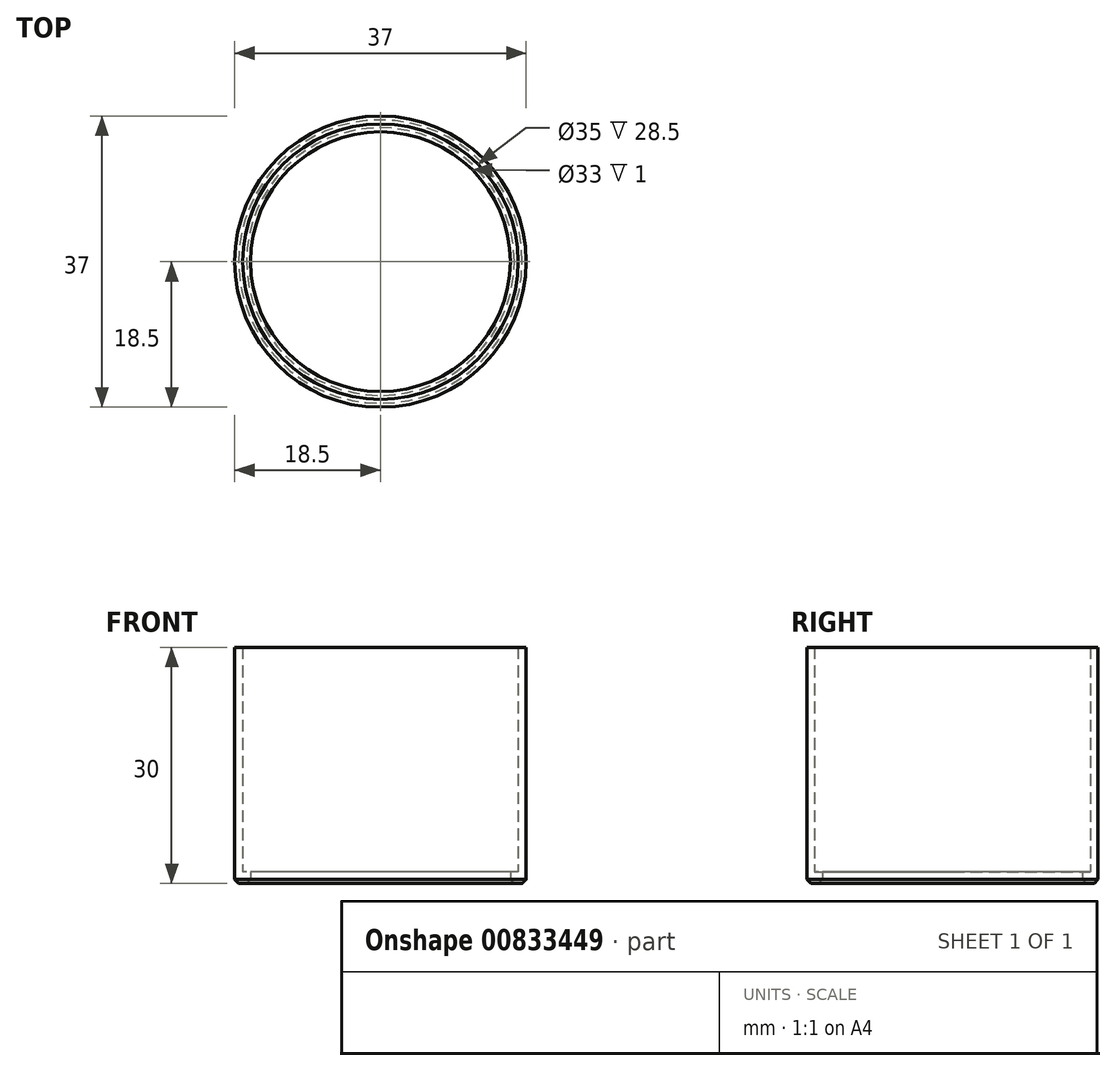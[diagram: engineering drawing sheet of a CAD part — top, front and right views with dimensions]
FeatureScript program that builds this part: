
annotation { "Feature Type Name" : "Feature", "Feature Type Description" : "" }
export const myFeature = defineFeature(function(context is Context, id is Id, definition is map)
    precondition{}
    {
        {
            var Q0;
            Q0=qCreatedBy(makeId("Top.planeOp"),FACE);
            var sketch = newSketch(context, id + "F0", { "sketchPlane" : qUnion([Q0])});
            skCircle(sketch, "E0", {"center": v(0, 0) * mm, "radius": 16.5 * mm});
            skCircle(sketch, "E1", {"center": v(0, 0) * mm, "radius": 17.5 * mm});
            skCircle(sketch, "E2", {"center": v(0, 0) * mm, "radius": 18.5 * mm});
            skSolve(sketch);
        }
        {
            var Q0;
            Q0 = qSketchRegion(id + "F0", true);
            extrude(context, id + "F1", {"entities" : qUnion([Q0]), "depth" : 30 * mm, "offsetDistance" : 25 * mm});
        }
        {
            var Q0;
            Q0=makeQuery(id+"F0.imprint","IMPRINT",FACE,{"disambiguationData":[TD([[makeQuery(id+"F0.imprint","IMPRINT",EDGE,{"derivedFrom":sQuery(id+"F0.wireOp",EDGE,"E0")}),-1.0]])]});
            extrude(context, id + "F2", {"entities" : qUnion([Q0]), "operationType" : NewBodyOperationType.ADD, "depth" : 1.5 * mm, "offsetDistance" : 25 * mm});
        }
        {
            var Q0;
            Q0=makeQuery(id+"F1.opExtrude","CAP_EDGE",EDGE,{"disambiguationData":[OSD([sQuery(id+"F0.wireOp",EDGE,"E2")])],"isStart":true});
            var Q1;
            Q1=makeQuery(id+"F2.opExtrude","CAP_EDGE",EDGE,{"disambiguationData":[OSD([sQuery(id+"F0.wireOp",EDGE,"E0")])],"isStart":true});
            chamfer(context, id + "F3", {"entities" : qUnion([Q0, Q1]), "width" : .5 * mm, "tangentPropagation" : true});
        }
    });
